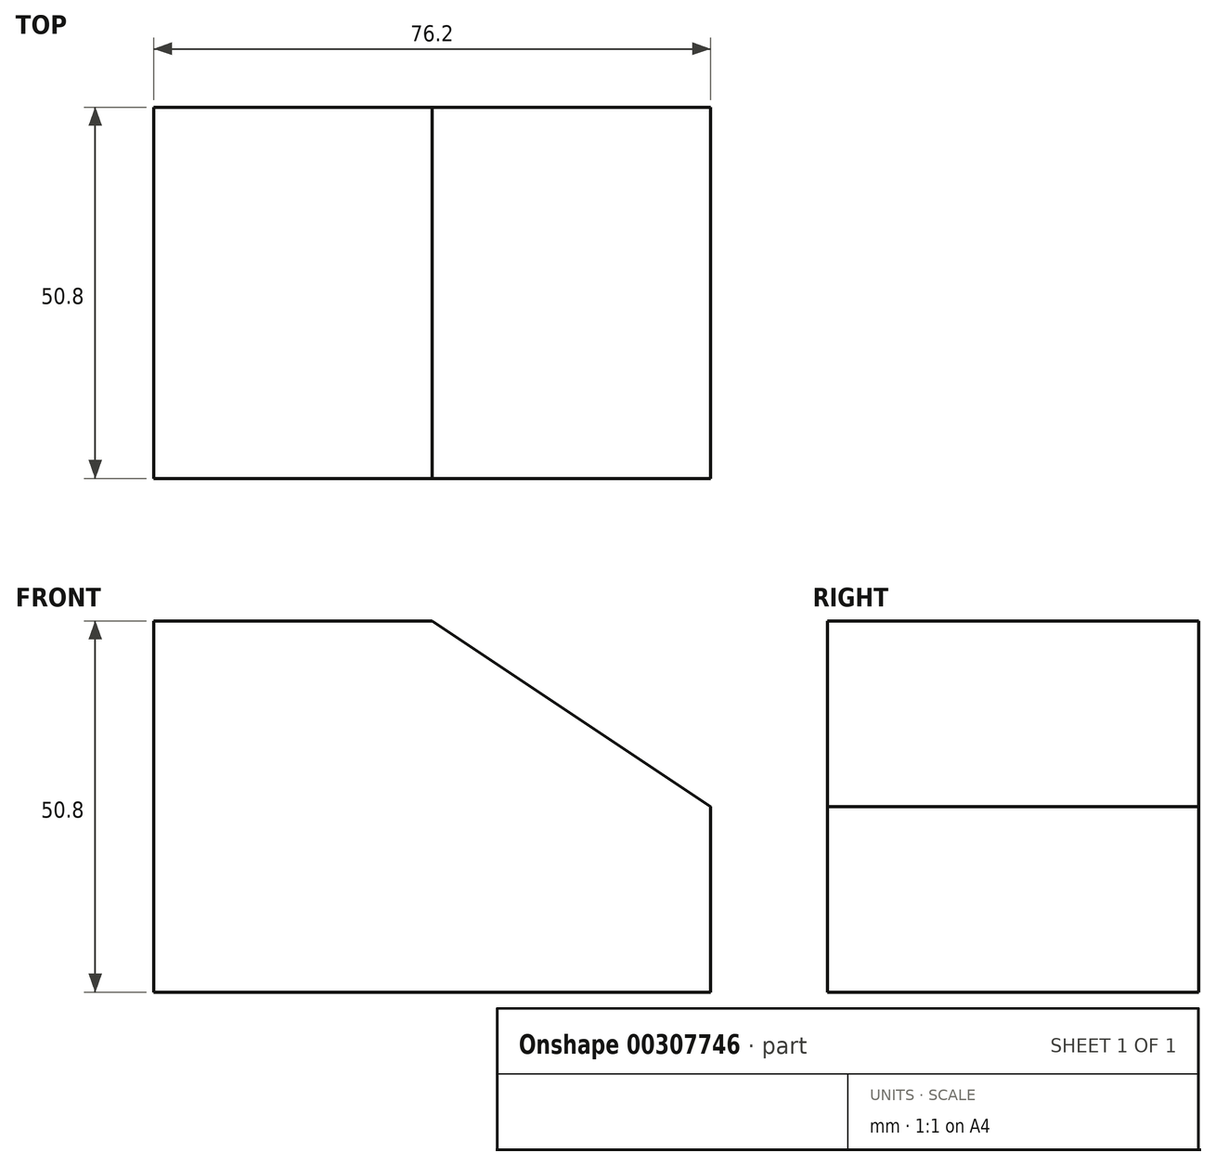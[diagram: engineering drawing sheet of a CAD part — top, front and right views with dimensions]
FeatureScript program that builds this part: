
annotation { "Feature Type Name" : "Feature", "Feature Type Description" : "" }
export const myFeature = defineFeature(function(context is Context, id is Id, definition is map)
    precondition{}
    {
        {
            var Q0;
            Q0=qCreatedBy(makeId("Front.planeOp"),FACE);
            var sketch = newSketch(context, id + "F0", { "sketchPlane" : qUnion([Q0])});
            skLineSegment(sketch, "E0", {"start": v(-31.75, -57.41) * mm, "end": v(44.45, -57.41) * mm});
            skLineSegment(sketch, "E1", {"start": v(44.45, -57.41) * mm, "end": v(44.45, -32.01) * mm});
            skLineSegment(sketch, "E2", {"start": v(-31.75, -57.41) * mm, "end": v(-31.75, -6.61) * mm});
            skLineSegment(sketch, "E3", {"start": v(-31.75, -6.61) * mm, "end": v(6.35, -6.61) * mm});
            skLineSegment(sketch, "E4", {"start": v(6.35, -6.61) * mm, "end": v(44.45, -32.01) * mm});
            skSolve(sketch);
        }
        {
            var Q0;
            Q0 = qSketchRegion(id + "F0", true);
            extrude(context, id + "F1", {"entities" : qUnion([Q0]), "depth" : 50.8 * mm});
        }
    });
